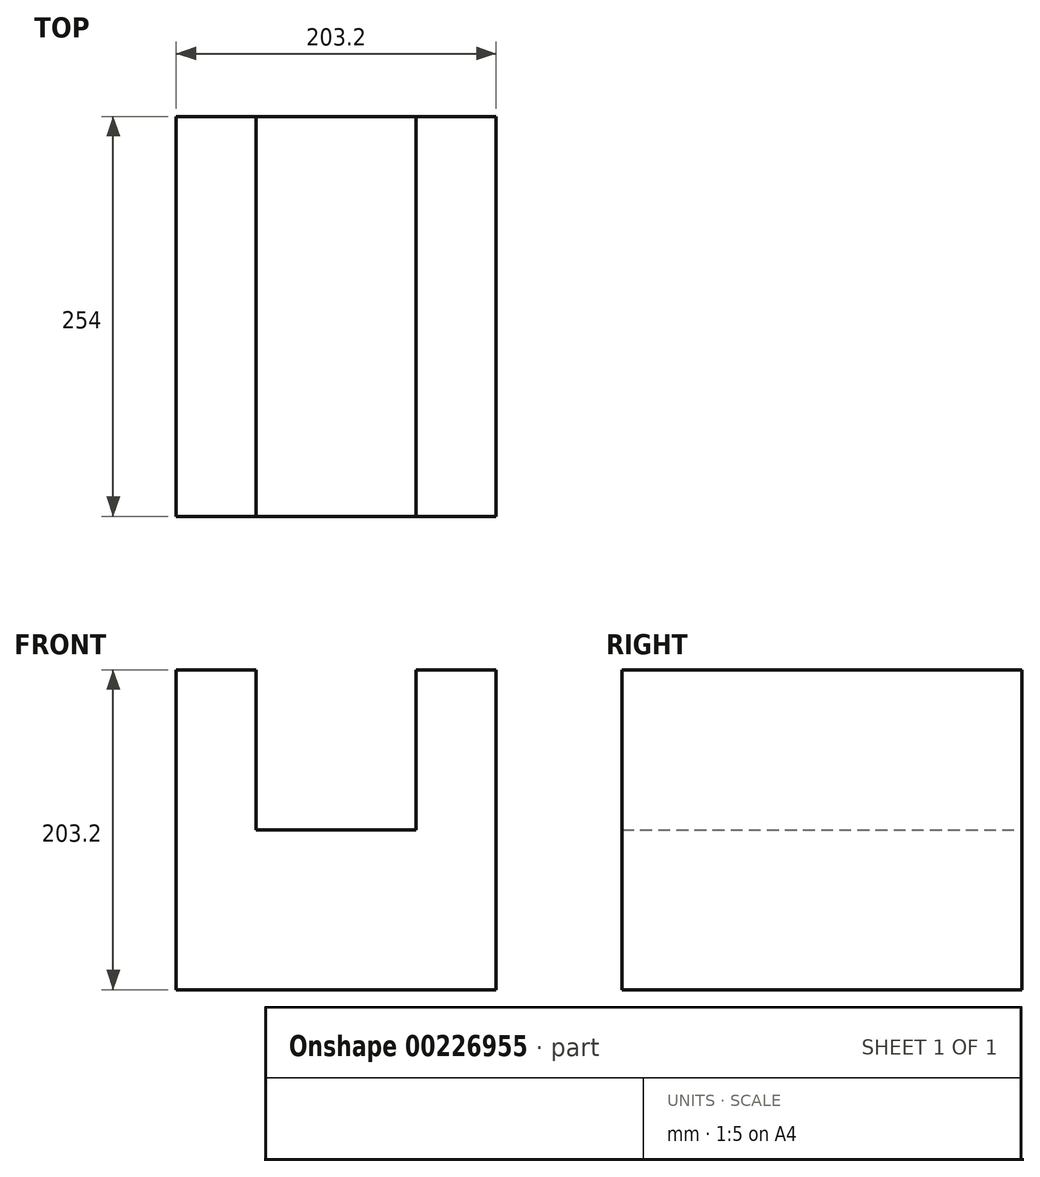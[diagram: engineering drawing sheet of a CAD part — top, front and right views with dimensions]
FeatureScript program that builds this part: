
annotation { "Feature Type Name" : "Feature", "Feature Type Description" : "" }
export const myFeature = defineFeature(function(context is Context, id is Id, definition is map)
    precondition{}
    {
        {
            var Q0;
            Q0=qCreatedBy(makeId("Front.planeOp"),FACE);
            var sketch = newSketch(context, id + "F0", { "sketchPlane" : qUnion([Q0])});
            skLineSegment(sketch, "E0.bottom", {"start": v(-188.08, 112.7) * mm, "end": v(-137.28, 112.7) * mm});
            skLineSegment(sketch, "E0.top", {"start": v(-188.08, -90.5) * mm, "end": v(15.12, -90.5) * mm});
            skLineSegment(sketch, "E0.left", {"start": v(-188.08, 112.7) * mm, "end": v(-188.08, -90.5) * mm});
            skLineSegment(sketch, "E0.right", {"start": v(15.12, 112.7) * mm, "end": v(15.12, -90.5) * mm});
            skLineSegment(sketch, "E1", {"start": v(-137.28, 112.7) * mm, "end": v(-137.28, 11.1) * mm});
            skLineSegment(sketch, "E2", {"start": v(-137.28, 11.1) * mm, "end": v(-35.68, 11.1) * mm});
            skLineSegment(sketch, "E3", {"start": v(-35.68, 11.1) * mm, "end": v(-35.68, 98.92) * mm});
            skLineSegment(sketch, "E4", {"start": v(-35.68, 98.92) * mm, "end": v(-35.68, 112.7) * mm});
            skLineSegment(sketch, "E5.trimOffspring", {"start": v(-35.68, 112.7) * mm, "end": v(15.12, 112.7) * mm});
            skSolve(sketch);
        }
        {
            var Q0;
            Q0=makeQuery(id+"F0.imprint","IMPRINT",FACE,{"disambiguationData":[TD([[makeQuery(id+"F0.imprint","IMPRINT",EDGE,{"derivedFrom":sQuery(id+"F0.wireOp",EDGE,"E0.bottom")}),-1.0]])]});
            extrude(context, id + "F1", {"entities" : qUnion([Q0]), "depth" : 254 * mm});
        }
    });
